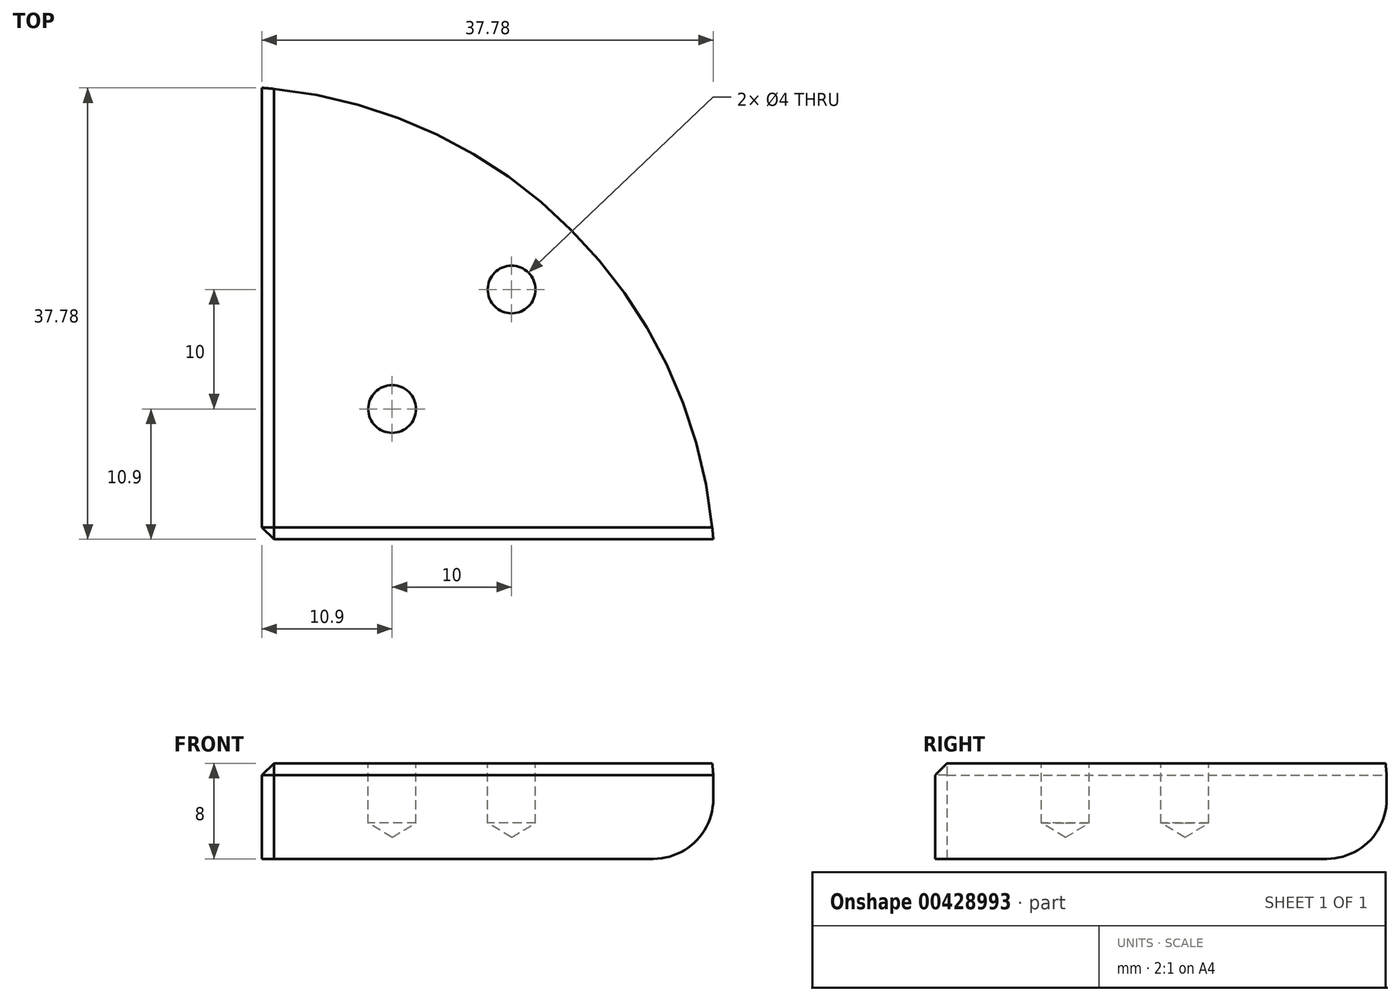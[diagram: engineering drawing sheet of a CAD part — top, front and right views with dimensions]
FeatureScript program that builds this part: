
annotation { "Feature Type Name" : "Feature", "Feature Type Description" : "" }
export const myFeature = defineFeature(function(context is Context, id is Id, definition is map)
    precondition{}
    {
        {
            var Q0;
            Q0=qCreatedBy(makeId("Top.planeOp"),FACE);
            var sketch = newSketch(context, id + "F0", { "sketchPlane" : qUnion([Q0])});
            skArc(sketch, "E0", {"start": v(40.88, 3.1) * mm, "mid": v(29, 29) * mm, "end": v(3.1, 40.88) * mm});
            skLineSegment(sketch, "E1", {"start": v(3.1, 3.1) * mm, "end": v(3.1, 40.88) * mm});
            skLineSegment(sketch, "E2", {"start": v(3.1, 3.1) * mm, "end": v(40.88, 3.1) * mm});
            skSolve(sketch);
        }
        {
            var Q0;
            Q0=qSketchRegion(id+"F0",true);
            extrude(context, id + "F1", {"entities" : qUnion([Q0]), "depth" : 8 * mm});
        }
        {
            var Q0;
            Q0=makeQuery(id+"F1.opExtrude","CAP_FACE",FACE,{"disambiguationData":[OSD([sQuery(id+"F0.wireOp",EDGE,"E0")])],"isStart":false});
            var sketch = newSketch(context, id + "F2", { "sketchPlane" : qUnion([Q0])});
            skLineSegment(sketch, "E3", {"start": v(0, 0) * mm, "end": v(33.6, 33.6) * mm, "construction": true});
            skCircle(sketch, "E4", {"center": v(14, 14) * mm, "radius": 2 * mm});
            skCircle(sketch, "E5", {"center": v(24, 24) * mm, "radius": 2 * mm});
            skSolve(sketch);
        }
        {
            var Q0;
            Q0=sQuery(id+"F2.wireOp",VERTEX,"E4.center");
            var Q1;
            Q1=sQuery(id+"F2.wireOp",VERTEX,"E5.center");
            var Q2;
            Q2=makeQuery(id+"F1.opExtrude","SWEPT_BODY",BODY,{"disambiguationData":[OSD([sQuery(id+"F0.wireOp",EDGE,"E0")])]});
            hole(context, id + "F3", {"style" : HoleStyle.SIMPLE, "endStyle" : HoleEndStyle.BLIND, "holeDiameter" : 4 * mm, "holeDepth" : 5 * mm, "isTappedThrough" : true, "tappedDepth" : 12 * mm, "tapClearance" : 3, "startFromSketch" : true, "locations" : qUnion([Q0, Q1]), "scope" : qUnion([Q2])});
        }
        {
            var Q0;
            Q0=makeQuery(id+"F1.opExtrude","SWEPT_EDGE",EDGE,{"disambiguationData":[OSD([sQuery(id+"F0.wireOp",EDGE,"E1"),sQuery(id+"F0.wireOp",EDGE,"E2")])]});
            var Q1;
            Q1=makeQuery(id+"F1.opExtrude","CAP_EDGE",EDGE,{"disambiguationData":[OSD([sQuery(id+"F0.wireOp",EDGE,"E2")])],"isStart":false});
            var Q2;
            Q2=makeQuery(id+"F1.opExtrude","CAP_EDGE",EDGE,{"disambiguationData":[OSD([sQuery(id+"F0.wireOp",EDGE,"E1")])],"isStart":false});
            chamfer(context, id + "F4", {"entities" : qUnion([Q0, Q1, Q2]), "width" : 1 * mm, "tangentPropagation" : true});
        }
        {
            var Q0;
            Q0=makeQuery(id+"F1.opExtrude","CAP_EDGE",EDGE,{"disambiguationData":[OSD([sQuery(id+"F0.wireOp",EDGE,"E0")])],"isStart":true});
            fillet(context, id + "F5", {"entities" : qUnion([Q0]), "radius" : 5 * mm, "tangentPropagation" : true, "allowEdgeOverflow" : false});
        }
    });
